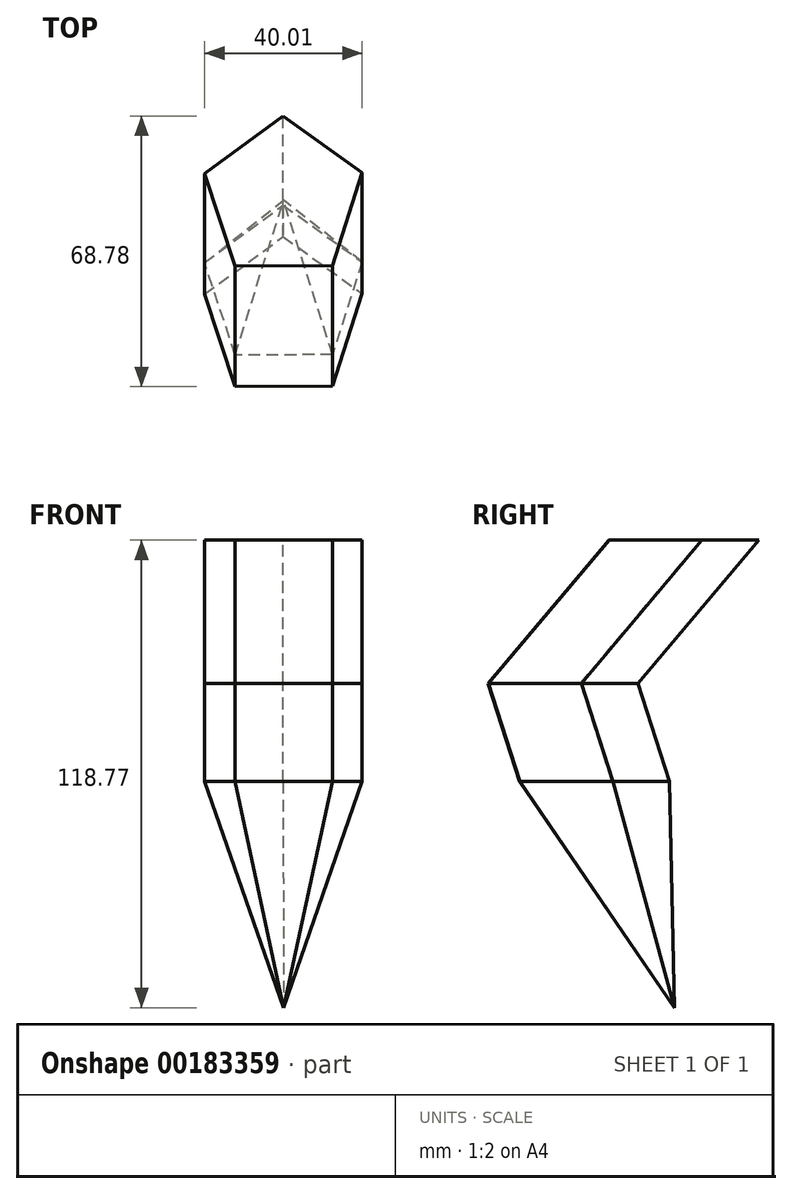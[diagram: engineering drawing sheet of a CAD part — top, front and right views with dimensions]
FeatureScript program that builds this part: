
annotation { "Feature Type Name" : "Feature", "Feature Type Description" : "" }
export const myFeature = defineFeature(function(context is Context, id is Id, definition is map)
    precondition{}
    {
        {
            var Q0;
            Q0=qCreatedBy(makeId("Top.planeOp"),FACE);
            var sketch = newSketch(context, id + "F0", { "sketchPlane" : qUnion([Q0])});
            skCircle(sketch, "E0.cCircle", {"center": v(0, 0) * mm, "radius": 17.02 * mm, "construction": true});
            skLineSegment(sketch, "E0.0", {"start": v(-20.04, 6.4) * mm, "end": v(-0.1, 21.03) * mm});
            skLineSegment(sketch, "E0.1", {"start": v(-0.1, 21.03) * mm, "end": v(19.97, 6.6) * mm});
            skLineSegment(sketch, "E0.2", {"start": v(19.97, 6.6) * mm, "end": v(12.45, -16.96) * mm});
            skLineSegment(sketch, "E0.3", {"start": v(12.45, -16.96) * mm, "end": v(-12.28, -17.08) * mm});
            skLineSegment(sketch, "E0.4", {"start": v(-12.28, -17.08) * mm, "end": v(-20.04, 6.4) * mm});
            skPoint(sketch, "E0.0.midPoint", {"position": v(-10.07, 13.72) * mm});
            skSolve(sketch);
        }
        {
            var Q0;
            Q0=qCreatedBy(makeId("Right.planeOp"),FACE);
            var sketch = newSketch(context, id + "F1", { "sketchPlane" : qUnion([Q0])});
            skPoint(sketch, "E1", {"position": v(39.05, 25.68) * mm});
            skPoint(sketch, "E2", {"position": v(22.65, 61.35) * mm});
            skPoint(sketch, "E3", {"position": v(-8.02, 24.97) * mm});
            skPoint(sketch, "E4", {"position": v(-36.2, 66.34) * mm});
            skPoint(sketch, "E5", {"position": v(42.62, -17.83) * mm});
            skPoint(sketch, "E6", {"position": v(22.3, -57.42) * mm});
            skPoint(sketch, "E7", {"position": v(-10.88, -20.33) * mm});
            skPoint(sketch, "E8", {"position": v(-50.11, -48.15) * mm});
            skLineSegment(sketch, "E9", {"start": v(0, 0) * mm, "end": v(-8.02, 24.97) * mm});
            skLineSegment(sketch, "E10", {"start": v(-8.02, 24.97) * mm, "end": v(-36.2, 66.34) * mm});
            skLineSegment(sketch, "E11", {"start": v(-8.02, 24.97) * mm, "end": v(22.65, 61.35) * mm});
            skLineSegment(sketch, "E12", {"start": v(0, 0) * mm, "end": v(39.05, 25.68) * mm});
            skSolve(sketch);
        }
        {
            var Q0;
            Q0=makeQuery(id+"F0.imprint","IMPRINT",FACE,{"disambiguationData":[TD([[makeQuery(id+"F0.imprint","IMPRINT",EDGE,{"derivedFrom":sQuery(id+"F0.wireOp",EDGE,"E0.0")}),-1.0]])]});
            var Q1;
            Q1=sQuery(id+"F1.wireOp",EDGE,"E9");
            sweep(context, id + "F2", {"profiles" : qUnion([Q0]), "path" : qUnion([Q1])});
        }
        {
            var Q0;
            Q0=makeQuery(id+"F2.opSweep","CAP_FACE",FACE,{"disambiguationData":[OSD([sQuery(id+"F0.wireOp",EDGE,"E0.0"),sQuery(id+"F0.wireOp",EDGE,"E0.1"),sQuery(id+"F0.wireOp",EDGE,"E0.2"),sQuery(id+"F0.wireOp",EDGE,"E0.3"),sQuery(id+"F0.wireOp",EDGE,"E0.4"),sQuery(id+"F1.wireOp",VERTEX,"E9.end")])],"isStart":false});
            var Q1;
            Q1=sQuery(id+"F1.wireOp",EDGE,"E11");
            sweep(context, id + "F3", {"operationType" : NewBodyOperationType.ADD, "profiles" : qUnion([Q0]), "path" : qUnion([Q1])});
        }
        {
            var Q1;
            Q1=makeQuery(id+"F2.opSweep","CAP_FACE",FACE,{"disambiguationData":[OSD([sQuery(id+"F0.wireOp",EDGE,"E0.0"),sQuery(id+"F0.wireOp",EDGE,"E0.1"),sQuery(id+"F0.wireOp",EDGE,"E0.2"),sQuery(id+"F0.wireOp",EDGE,"E0.3"),sQuery(id+"F0.wireOp",EDGE,"E0.4"),sQuery(id+"F1.wireOp",VERTEX,"E9.start")])],"isStart":true});
            var Q2;
            Q2=sQuery(id+"F1.wireOp",VERTEX,"E6");
            loft(context, id + "F4", {"operationType" : NewBodyOperationType.ADD, "sheetProfilesArray" : [{ "sheetProfileEntities" : qUnion([Q1]) }, { "sheetProfileEntities" : qUnion([Q2]) }]});
        }
    });
